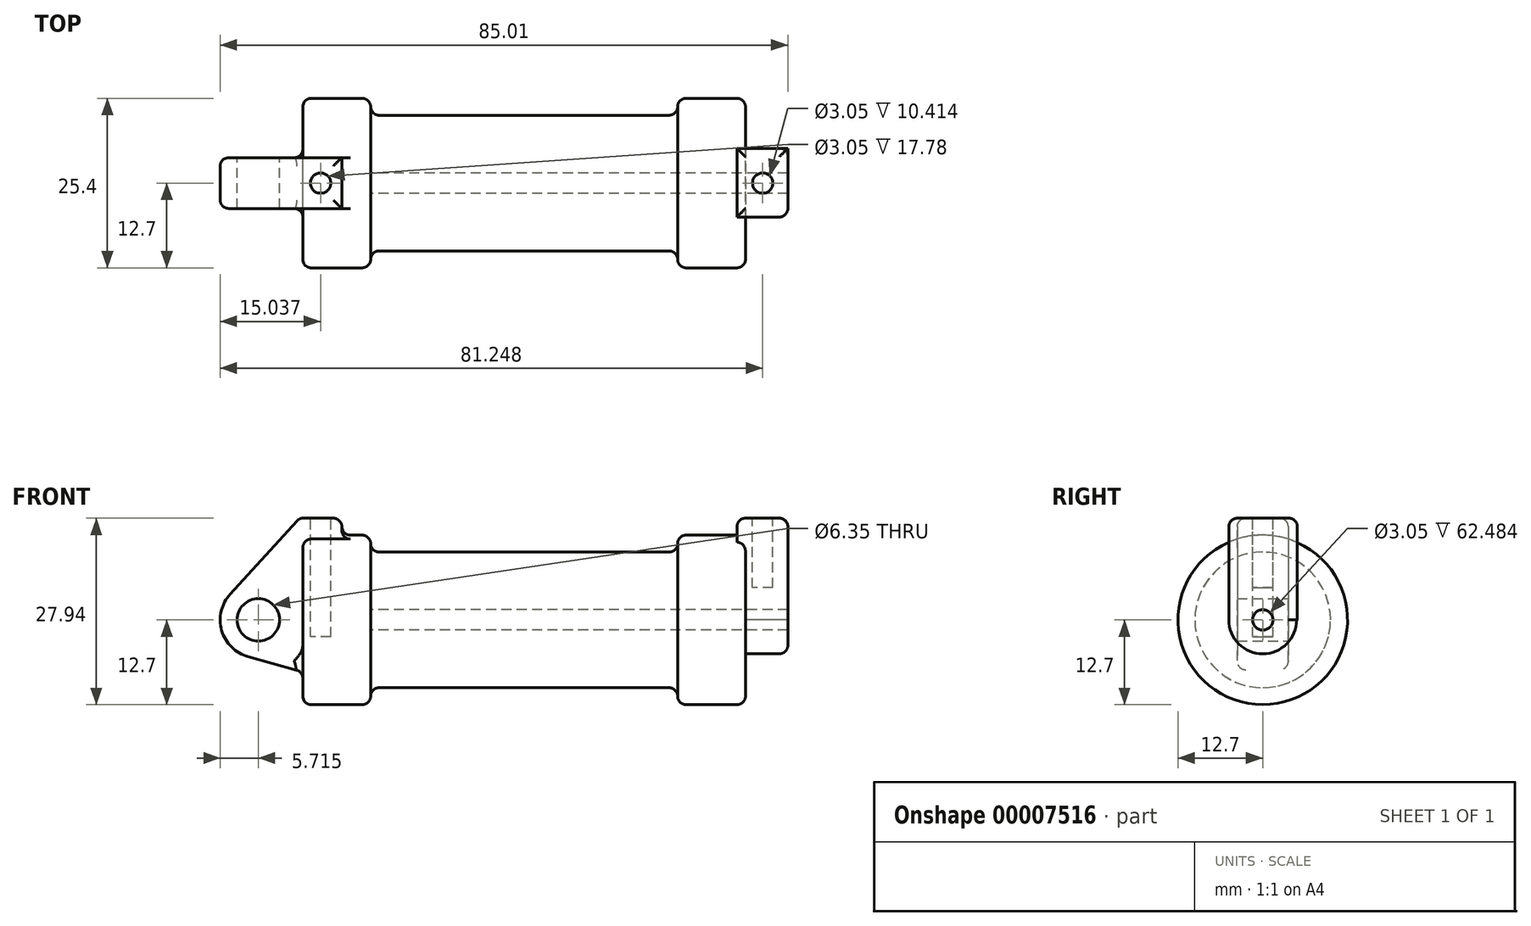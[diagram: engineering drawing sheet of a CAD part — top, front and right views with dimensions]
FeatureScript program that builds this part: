
annotation { "Feature Type Name" : "Feature", "Feature Type Description" : "" }
export const myFeature = defineFeature(function(context is Context, id is Id, definition is map)
    precondition{}
    {
        {
            var Q0;
            Q0=qCreatedBy(makeId("Front.planeOp"),FACE);
            var sketch = newSketch(context, id + "F0", { "sketchPlane" : qUnion([Q0])});
            skLineSegment(sketch, "E0", {"start": v(0, 0) * mm, "end": v(0, 12.7) * mm});
            skLineSegment(sketch, "E1", {"start": v(0, 12.7) * mm, "end": v(10.16, 12.7) * mm});
            skLineSegment(sketch, "E2", {"start": v(10.16, 12.7) * mm, "end": v(10.16, 10.16) * mm});
            skLineSegment(sketch, "E3", {"start": v(10.16, 10.16) * mm, "end": v(56.13, 10.16) * mm});
            skLineSegment(sketch, "E4", {"start": v(56.13, 10.16) * mm, "end": v(56.13, 12.7) * mm});
            skLineSegment(sketch, "E5", {"start": v(56.13, 12.7) * mm, "end": v(66.3, 12.7) * mm});
            skLineSegment(sketch, "E6", {"start": v(66.3, 12.7) * mm, "end": v(66.3, 0) * mm});
            skLineSegment(sketch, "E7", {"start": v(66.3, 0) * mm, "end": v(0, 0) * mm});
            skLineSegment(sketch, "E8", {"start": v(5.84, 15.24) * mm, "end": v(-0.5, 15.24) * mm});
            skLineSegment(sketch, "E9", {"start": v(-0.5, 15.24) * mm, "end": v(-10.88, 3.85) * mm});
            skLineSegment(sketch, "E10", {"start": v(0, 0) * mm, "end": v(-6.65, 0) * mm});
            skCircle(sketch, "E11", {"center": v(-6.65, 0) * mm, "radius": 5.72 * mm});
            skCircle(sketch, "E12", {"center": v(-6.65, 0) * mm, "radius": 3.18 * mm});
            skLineSegment(sketch, "E13", {"start": v(5.84, 15.24) * mm, "end": v(5.84, -9.4) * mm});
            skLineSegment(sketch, "E14", {"start": v(5.84, -9.4) * mm, "end": v(-8.18, -5.5) * mm});
            skSolve(sketch);
        }
        {
            var Q0;
            {var subQ6=sQuery(id+"F0.wireOp",EDGE,"E2");Q0=makeQuery(id+"F0.imprint","IMPRINT",FACE,{"disambiguationData":[TD([[makeQuery(id+"F0.imprint","IMPRINT",EDGE,{"derivedFrom":subQ6}),-1.0]])]});}
            var Q1;
            {var subQ5=sQuery(id+"F0.wireOp",EDGE,"E0");Q1=makeQuery(id+"F0.imprint","IMPRINT",FACE,{"disambiguationData":[TD([[makeQuery(id+"F0.imprint","IMPRINT",EDGE,{"derivedFrom":subQ5}),-1.0]])]});}
            var Q2;
            Q2=sQuery(id+"F0.wireOp",EDGE,"E7");
            revolve(context, id + "F1", {"entities" : qUnion([Q0, Q1]), "axis" : qUnion([Q2]), "revolveType" : RevolveType.FULL});
        }
        {
            var Q0;
            {var subQ8=sQuery(id+"F0.wireOp",EDGE,"E0");Q0=makeQuery(id+"F0.imprint","IMPRINT",FACE,{"disambiguationData":[TD([[makeQuery(id+"F0.imprint","IMPRINT",EDGE,{"derivedFrom":subQ8}),1.0]])]});}
            var Q1;
            {var subQ0=sQuery(id+"F0.wireOp",EDGE,"E12");Q1=makeQuery(id+"F0.imprint","IMPRINT",FACE,{"disambiguationData":[TD([[makeQuery(id+"F0.imprint","IMPRINT",EDGE,{"derivedFrom":subQ0}),-1.0]])]});}
            var Q2;
            {var subQ0=sQuery(id+"F0.wireOp",EDGE,"E14");Q2=makeQuery(id+"F0.imprint","IMPRINT",FACE,{"disambiguationData":[TD([[makeQuery(id+"F0.imprint","IMPRINT",EDGE,{"derivedFrom":subQ0}),-1.0]])]});}
            var Q3;
            {var subQ5=sQuery(id+"F0.wireOp",EDGE,"E0");Q3=makeQuery(id+"F0.imprint","IMPRINT",FACE,{"disambiguationData":[TD([[makeQuery(id+"F0.imprint","IMPRINT",EDGE,{"derivedFrom":subQ5}),-1.0]])]});}
            extrude(context, id + "F2", {"entities" : qUnion([Q0, Q1, Q2, Q3]), "operationType" : NewBodyOperationType.ADD, "endBound" : BoundingType.SYMMETRIC, "depth" : 7.62 * mm});
        }
        {
            var Q0;
            Q0=makeQuery(id+"F1.opRevolve","SWEPT_FACE",FACE,{"disambiguationData":[OSD([sQuery(id+"F0.wireOp",EDGE,"E6")])]});
            var sketch = newSketch(context, id + "F3", { "sketchPlane" : qUnion([Q0])});
            skCircle(sketch, "E15", {"center": v(0, 0) * mm, "radius": 1.52 * mm});
            skCircle(sketch, "E16", {"center": v(0, 0) * mm, "radius": 5.08 * mm});
            skLineSegment(sketch, "E17.bottom", {"start": v(-5.08, 0) * mm, "end": v(5.2, 0) * mm});
            skLineSegment(sketch, "E17.top", {"start": v(-5.08, 15.24) * mm, "end": v(5.2, 15.24) * mm});
            skLineSegment(sketch, "E17.left", {"start": v(-5.08, 0) * mm, "end": v(-5.08, 15.24) * mm});
            skLineSegment(sketch, "E17.right", {"start": v(5.2, 0) * mm, "end": v(5.2, 15.24) * mm});
            skSolve(sketch);
        }
        {
            var Q0;
            {var subQ0=sQuery(id+"F3.wireOp",EDGE,"E17.bottom");var subQ3=sQuery(id+"F3.wireOp",EDGE,"E15");var subQ5=makeQuery(id+"F3.imprint","INTERSECT",VERTEX,{"disambiguationData":[OD(0.0)],"derivedFrom":[subQ3,subQ0]});Q0=makeQuery(id+"F3.imprint","IMPRINT",FACE,{"disambiguationData":[TD([[makeQuery(id+"F3.imprint","IMPRINT",EDGE,{"disambiguationData":[TD([[subQ5,-1.0]])],"derivedFrom":subQ3}),-1.0]])]});}
            var Q1;
            {var subQ0=sQuery(id+"F3.wireOp",EDGE,"E17.bottom");var subQ3=sQuery(id+"F3.wireOp",EDGE,"E15");var subQ5=makeQuery(id+"F3.imprint","INTERSECT",VERTEX,{"disambiguationData":[OD(0.0)],"derivedFrom":[subQ3,subQ0]});Q1=makeQuery(id+"F3.imprint","IMPRINT",FACE,{"disambiguationData":[TD([[makeQuery(id+"F3.imprint","IMPRINT",EDGE,{"disambiguationData":[TD([[subQ5,1.0]])],"derivedFrom":subQ3}),-1.0]])]});}
            var Q2;
            {var subQ1=sQuery(id+"F3.wireOp",EDGE,"E17.right");var subQ5=sQuery(id+"F3.wireOp",EDGE,"E17.bottom");var subQ6=makeQuery(id+"F3.imprint","INTERSECT",VERTEX,{"derivedFrom":[subQ5,subQ1]});Q2=makeQuery(id+"F3.imprint","IMPRINT",FACE,{"disambiguationData":[TD([[makeQuery(id+"F3.imprint","IMPRINT",EDGE,{"disambiguationData":[TD([[subQ6,1.0]])],"derivedFrom":subQ5}),1.0]])]});}
            var Q3;
            {var subQ5=sQuery(id+"F3.wireOp",EDGE,"E17.top");Q3=makeQuery(id+"F3.imprint","IMPRINT",FACE,{"disambiguationData":[TD([[makeQuery(id+"F3.imprint","IMPRINT",EDGE,{"derivedFrom":subQ5}),-1.0]])]});}
            extrude(context, id + "F4", {"entities" : qUnion([Q0, Q1, Q2, Q3]), "operationType" : NewBodyOperationType.ADD, "depth" : 6.35 * mm});
        }
        {
            var Q0;
            Q0=makeQuery(id+"F4.opExtrude","CAP_FACE",FACE,{"disambiguationData":[OSD([sQuery(id+"F3.wireOp",EDGE,"E15"),sQuery(id+"F3.wireOp",EDGE,"E16"),sQuery(id+"F3.wireOp",EDGE,"E17.bottom"),sQuery(id+"F3.wireOp",EDGE,"E17.top"),sQuery(id+"F3.wireOp",EDGE,"E17.left"),sQuery(id+"F3.wireOp",EDGE,"E17.right")])],"isStart":true});
            extrude(context, id + "F5", {"entities" : qUnion([Q0]), "operationType" : NewBodyOperationType.ADD, "depth" : 1.27 * mm});
        }
        {
            var Q0;
            Q0=makeQuery(id+"F4.boolean.opBoolean","SPLIT",FACE,{"disambiguationData":[TD([makeQuery(id+"F4.opExtrude","SWEPT_FACE",FACE,{"disambiguationData":[OSD([sQuery(id+"F3.wireOp",EDGE,"E15")])]})])],"derivedFrom":makeQuery(id+"F1.opRevolve","SWEPT_FACE",FACE,{"disambiguationData":[OSD([sQuery(id+"F0.wireOp",EDGE,"E6")])]})});
            var Q1;
            Q1=makeQuery(id+"F1.opRevolve","SWEPT_FACE",FACE,{"disambiguationData":[OSD([sQuery(id+"F0.wireOp",EDGE,"E2")])]});
            extrude(context, id + "F6", {"entities" : qUnion([Q0]), "operationType" : NewBodyOperationType.REMOVE, "endBound" : BoundingType.UP_TO_SURFACE, "oppositeDirection" : true, "endBoundEntityFace" : qUnion([Q1]), "depth" : 25.4 * mm});
        }
        {
            var Q0;
            Q0=makeQuery(id+"F2.opExtrude","SWEPT_FACE",FACE,{"disambiguationData":[OSD([sQuery(id+"F0.wireOp",EDGE,"E8")])]});
            var sketch = newSketch(context, id + "F7", { "sketchPlane" : qUnion([Q0])});
            skLineSegment(sketch, "E18", {"start": v(5.84, -3.81) * mm, "end": v(-0.5, -3.81) * mm});
            skLineSegment(sketch, "E19", {"start": v(68.2, 0) * mm, "end": v(2.67, 0) * mm, "construction": true});
            skCircle(sketch, "E20", {"center": v(2.67, 0) * mm, "radius": 1.52 * mm});
            skSolve(sketch);
        }
        {
            var Q0;
            {var subQ0=sQuery(id+"F3.wireOp",EDGE,"E17.top");Q0=makeQuery(id+"F5.boolean.opBoolean","MERGE",FACE,{"derivedFrom":[makeQuery(id+"F4.opExtrude","SWEPT_FACE",FACE,{"disambiguationData":[OSD([subQ0])]}),makeQuery(id+"F5.opExtrude","SWEPT_FACE",FACE,{"disambiguationData":[OSD([subQ0])]})]});}
            var sketch = newSketch(context, id + "F8", { "sketchPlane" : qUnion([Q0])});
            skCircle(sketch, "E21", {"center": v(68.88, 0) * mm, "radius": 1.52 * mm});
            skSolve(sketch);
        }
        {
            var Q0;
            Q0=makeQuery(id+"F8.imprint","IMPRINT",FACE,{"disambiguationData":[TD([[makeQuery(id+"F8.imprint","IMPRINT",EDGE,{"derivedFrom":sQuery(id+"F8.wireOp",EDGE,"E21")}),1.0]])]});
            extrude(context, id + "F9", {"entities" : qUnion([Q0]), "operationType" : NewBodyOperationType.REMOVE, "oppositeDirection" : true, "depth" : 10.4 * mm});
        }
        {
            var Q0;
            Q0=makeQuery(id+"F7.imprint","IMPRINT",FACE,{"disambiguationData":[TD([[makeQuery(id+"F7.imprint","IMPRINT",EDGE,{"derivedFrom":sQuery(id+"F7.wireOp",EDGE,"E20")}),1.0]])]});
            var Q1;
            Q1=sQuery(id+"F7.wireOp",EDGE,"E20");
            extrude(context, id + "F10", {"entities" : qUnion([Q0]), "operationType" : NewBodyOperationType.REMOVE, "surfaceEntities" : qUnion([Q1]), "oppositeDirection" : true, "depth" : 17.78 * mm});
        }
        {
            var Q0;
            Q0=makeQuery(id+"F1.opRevolve","SWEPT_EDGE",EDGE,{"disambiguationData":[OSD([sQuery(id+"F0.wireOp",EDGE,"E2"),sQuery(id+"F0.wireOp",EDGE,"E3")])]});
            var Q1;
            Q1=makeQuery(id+"F1.opRevolve","SWEPT_EDGE",EDGE,{"disambiguationData":[OSD([sQuery(id+"F0.wireOp",EDGE,"E1"),sQuery(id+"F0.wireOp",EDGE,"E2")])]});
            var Q2;
            Q2=makeQuery(id+"F1.opRevolve","SWEPT_EDGE",EDGE,{"disambiguationData":[OSD([sQuery(id+"F0.wireOp",EDGE,"E0"),sQuery(id+"F0.wireOp",EDGE,"E1")])]});
            var Q3;
            Q3=makeQuery(id+"F4.boolean.opBoolean","SPLIT",EDGE,{"disambiguationData":[OD(1.0)],"derivedFrom":makeQuery(id+"F1.opRevolve","SWEPT_EDGE",EDGE,{"disambiguationData":[OSD([sQuery(id+"F0.wireOp",EDGE,"E5"),sQuery(id+"F0.wireOp",EDGE,"E6")])]})});
            var Q4;
            Q4=makeQuery(id+"F1.opRevolve","SWEPT_EDGE",EDGE,{"disambiguationData":[OSD([sQuery(id+"F0.wireOp",EDGE,"E4"),sQuery(id+"F0.wireOp",EDGE,"E5")])]});
            var Q5;
            Q5=makeQuery(id+"F1.opRevolve","SWEPT_EDGE",EDGE,{"disambiguationData":[OSD([sQuery(id+"F0.wireOp",EDGE,"E3"),sQuery(id+"F0.wireOp",EDGE,"E4")])]});
            var Q6;
            Q6=makeQuery(id+"F2.opExtrude","SWEPT_FACE",FACE,{"disambiguationData":[OSD([sQuery(id+"F0.wireOp",EDGE,"E14")])]});
            var Q7;
            Q7=makeQuery(id+"F2.opExtrude","CAP_EDGE",EDGE,{"disambiguationData":[OSD([sQuery(id+"F0.wireOp",EDGE,"E8")])],"isStart":true});
            var Q8;
            Q8=makeQuery(id+"F2.opExtrude","SWEPT_EDGE",EDGE,{"disambiguationData":[OSD([sQuery(id+"F0.wireOp",EDGE,"E8"),sQuery(id+"F0.wireOp",EDGE,"E13")])]});
            var Q9;
            Q9=makeQuery(id+"F2.opExtrude","CAP_EDGE",EDGE,{"disambiguationData":[OSD([sQuery(id+"F0.wireOp",EDGE,"E8")])],"isStart":false});
            var Q10;
            Q10=makeQuery(id+"F2.opExtrude","SWEPT_EDGE",EDGE,{"disambiguationData":[OSD([sQuery(id+"F0.wireOp",EDGE,"E8"),sQuery(id+"F0.wireOp",EDGE,"E9")])]});
            var Q11;
            Q11=makeQuery(id+"F2.boolean.opBoolean","INTERSECT",EDGE,{"derivedFrom":[makeQuery(id+"F1.opRevolve","SWEPT_FACE",FACE,{"disambiguationData":[OSD([sQuery(id+"F0.wireOp",EDGE,"E1")])]}),makeQuery(id+"F2.opExtrude","SWEPT_FACE",FACE,{"disambiguationData":[OSD([sQuery(id+"F0.wireOp",EDGE,"E13")])]})]});
            var Q12;
            {var subQ0=sQuery(id+"F3.wireOp",EDGE,"E17.left");var subQ1=sQuery(id+"F3.wireOp",EDGE,"E16");Q12=makeQuery(id+"F4.boolean.opBoolean","SPLIT",EDGE,{"disambiguationData":[TD([makeQuery(id+"F4.opExtrude","SWEPT_FACE",FACE,{"disambiguationData":[OSD([subQ1])]})])],"derivedFrom":makeQuery(id+"F4.opExtrude","CAP_EDGE",EDGE,{"disambiguationData":[OSD([subQ0])],"isStart":true})});}
            var Q13;
            Q13=makeQuery(id+"F4.opExtrude","CAP_EDGE",EDGE,{"disambiguationData":[OSD([sQuery(id+"F3.wireOp",EDGE,"E17.top")])],"isStart":false});
            var Q14;
            {var subQ0=sQuery(id+"F3.wireOp",EDGE,"E17.top");var subQ1=sQuery(id+"F3.wireOp",EDGE,"E17.right");Q14=makeQuery(id+"F5.boolean.opBoolean","MERGE",EDGE,{"derivedFrom":[makeQuery(id+"F4.opExtrude","SWEPT_EDGE",EDGE,{"disambiguationData":[OSD([subQ0,subQ1])]}),makeQuery(id+"F5.opExtrude","SWEPT_EDGE",EDGE,{"disambiguationData":[OSD([subQ0,subQ1])]})]});}
            var Q15;
            Q15=makeQuery(id+"F5.opExtrude","CAP_EDGE",EDGE,{"disambiguationData":[OSD([sQuery(id+"F3.wireOp",EDGE,"E17.top")])],"isStart":false});
            var Q16;
            {var subQ0=sQuery(id+"F3.wireOp",EDGE,"E17.top");var subQ1=sQuery(id+"F3.wireOp",EDGE,"E17.left");Q16=makeQuery(id+"F5.boolean.opBoolean","MERGE",EDGE,{"derivedFrom":[makeQuery(id+"F4.opExtrude","SWEPT_EDGE",EDGE,{"disambiguationData":[OSD([subQ0,subQ1])]}),makeQuery(id+"F5.opExtrude","SWEPT_EDGE",EDGE,{"disambiguationData":[OSD([subQ0,subQ1])]})]});}
            var Q17;
            Q17=makeQuery(id+"F4.opExtrude","CAP_EDGE",EDGE,{"disambiguationData":[OSD([sQuery(id+"F3.wireOp",EDGE,"E17.left")])],"isStart":false});
            fillet(context, id + "F11", {"entities" : qUnion([Q0, Q1, Q2, Q3, Q4, Q5, Q6, Q7, Q8, Q9, Q10, Q11, Q12, Q13, Q14, Q15, Q16, Q17]), "radius" : 1.27 * mm, "tangentPropagation" : true, "allowEdgeOverflow" : false});
        }
    });
